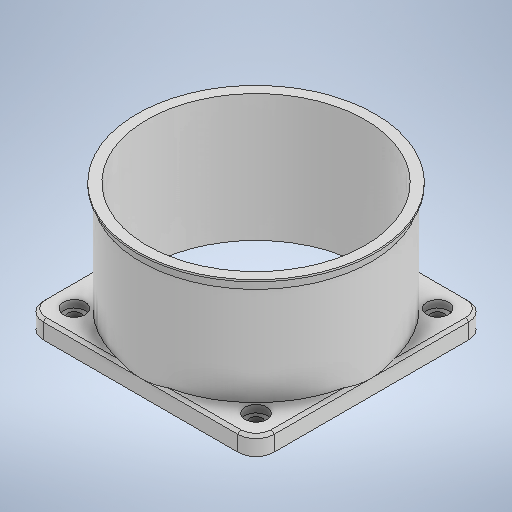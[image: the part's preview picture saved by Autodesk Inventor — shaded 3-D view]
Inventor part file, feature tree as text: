
AUTODESK INVENTOR PART (.ipt)
format: ipt  version: 2025.1 (Build 291241000, 241)  size: 316,416 bytes
history: native  units: in
note: dims shown in document units (in); Inventor stores cm internally (conversion verified against a paired STEP export)
features: sketch x5, extrude x3, chamfer x2, sweep x1
ambient origin geometry x8: Origin, YZ Plane, XZ Plane, XY Plane, X Axis, Y Axis, Z Axis, Center Point
bodies: Solid1 (feature_tree)
feature tree (11):
  extrude  "Extrusion1"  Depth=2.3622in
  extrude  "Extrusion2"  Depth=1.9685in
  sweep  "Sweep1"
  extrude  "Extrusion3"  Depth=0.1969in
  chamfer  "Chamfer1"  Distance=2.5in
  chamfer  "Chamfer2"  Distance=0.1969in
  sketch  "Sketch1"  dims[d1=0.1378in d2=2.3622in]
  sketch  "Sketch2"  dims[d3=1.9685in d4=1.9685in]
  sketch  "Sketch3"  dims[d5=0.9843in d6=0.9843in]
  sketch  "Sketch4"  dims[d7=0.1969in d8=0.1969in]
  sketch  "Sketch5"  dims[d9=2.5in d10=2.5in d11=0.1969in d12=0.0in d13=0.2362in d14=0.0787in d15=0.0in d16=180.0deg d17=1.1811in d18=0.7874in d19=0.3937in d20=0.0in d21=0.0in d22=0.0394in d23=0.1181in d24=0.0in d25=0.0394in d26=0.0984in d27=45.0deg d28=0.0295in d29=0.0787in d30=45.0deg]
